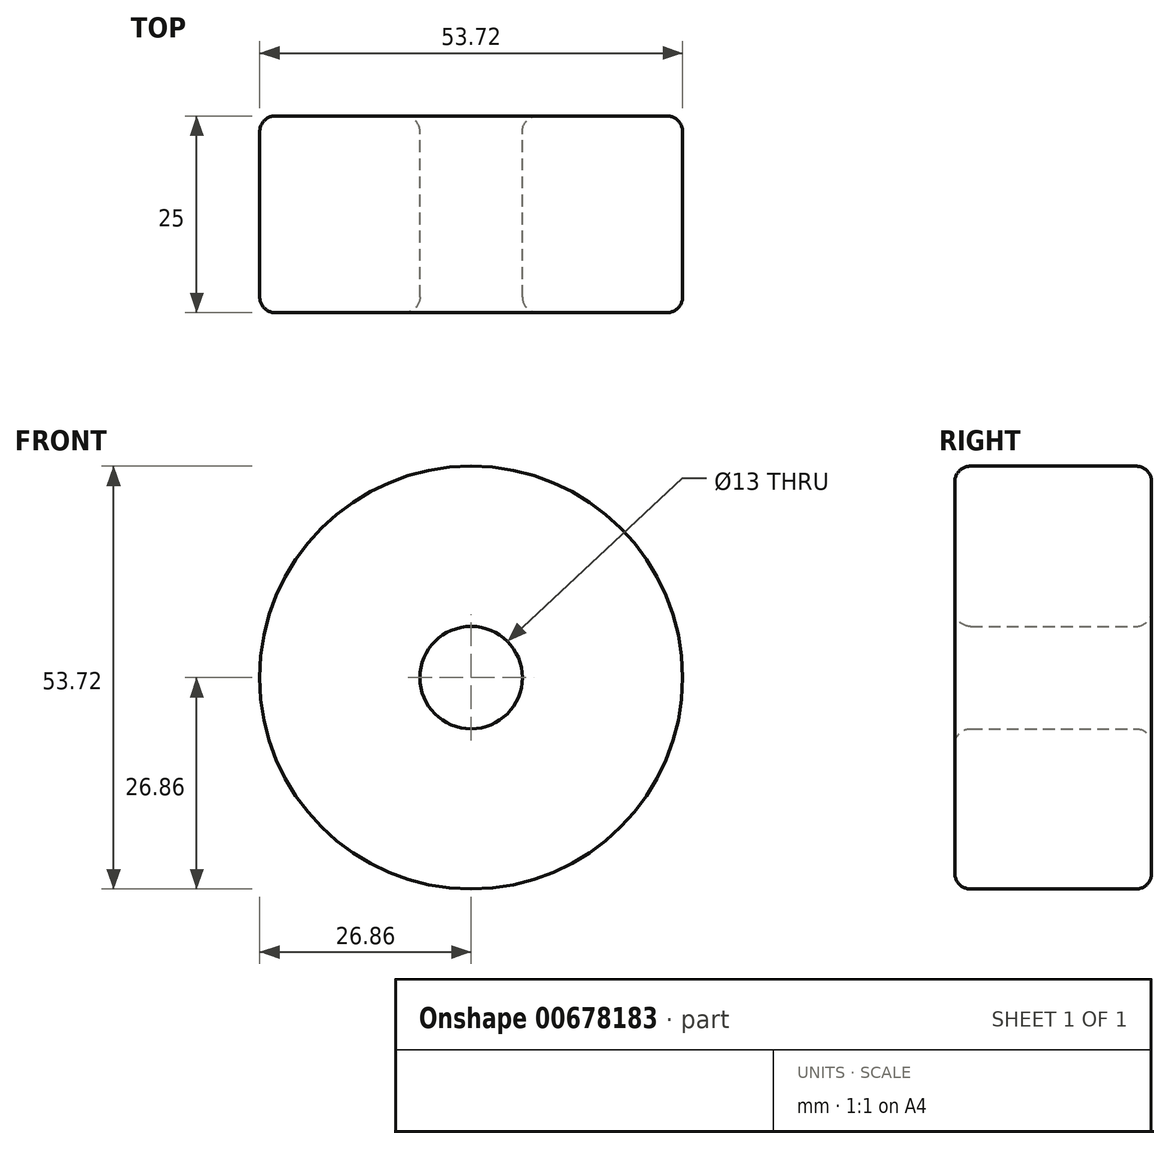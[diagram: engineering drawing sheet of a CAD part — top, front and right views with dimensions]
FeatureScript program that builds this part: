
annotation { "Feature Type Name" : "Feature", "Feature Type Description" : "" }
export const myFeature = defineFeature(function(context is Context, id is Id, definition is map)
    precondition{}
    {
        {
            var Q0;
            Q0=qCreatedBy(makeId("Front.planeOp"),FACE);
            var sketch = newSketch(context, id + "F0", { "sketchPlane" : qUnion([Q0])});
            skCircle(sketch, "E0", {"center": v(0, 0) * mm, "radius": 26.86 * mm});
            skCircle(sketch, "E1", {"center": v(0, 0) * mm, "radius": 29.34 * mm, "construction": true});
            skCircle(sketch, "E2", {"center": v(0, 0) * mm, "radius": 31.75 * mm, "construction": true});
            skLineSegment(sketch, "E3", {"start": v(0, 0) * mm, "end": v(0, 99.1) * mm, "construction": true});
            skLineSegment(sketch, "E4", {"start": v(0, 0) * mm, "end": v(-8, 122.09) * mm, "construction": true});
            skLineSegment(sketch, "E5", {"start": v(0, 29.34) * mm, "end": v(-120.67, 29.34) * mm, "construction": true});
            skLineSegment(sketch, "E6", {"start": v(0, 29.34) * mm, "end": v(-118.03, -13.62) * mm, "construction": true});
            skCircle(sketch, "E7", {"center": v(0, 0) * mm, "radius": 27.57 * mm, "construction": true});
            skCircle(sketch, "E8", {"center": v(0, 29.34) * mm, "radius": 14.6 * mm, "construction": true});
            skCircle(sketch, "E9", {"center": v(-13.72, 24.34) * mm, "radius": 14.6 * mm, "construction": true});
            skLineSegment(sketch, "E10", {"start": v(-4.16, 26.54) * mm, "end": v(-4.25, 26.52) * mm});
            skLineSegment(sketch, "E11", {"start": v(-4.25, 26.52) * mm, "end": v(-4.25, 26.52) * mm});
            skArc(sketch, "E12.MirrorCS", {"start": v(-4.25, 26.52) * mm, "mid": v(-4.23, 31.3) * mm, "end": v(-2.6, 35.79) * mm});
            skArc(sketch, "E13.MirrorCS", {"start": v(4.25, 26.52) * mm, "mid": v(4.23, 31.3) * mm, "end": v(2.6, 35.79) * mm});
            skLineSegment(sketch, "E14", {"start": v(-2.6, 35.79) * mm, "end": v(2.6, 35.79) * mm});
            skCircle(sketch, "E15", {"center": v(0, 0) * mm, "radius": 6.5 * mm});
            skSolve(sketch);
        }
        {
            var Q0;
            {var subQ1=sQuery(id+"F0.wireOp",EDGE,"NmizqAiV-zcEd-wW1i-qfzH-Hc12WR1YokAQ");Q0=makeQuery(id+"F0.imprint","IMPRINT",FACE,{"disambiguationData":[TD([[makeQuery(id+"F0.imprint","IMPRINT",EDGE,{"derivedFrom":subQ1}),1.0]])]});}
            var Q1;
            {var subQ0=sQuery(id+"F0.wireOp",EDGE,"E0");var subQ1=makeQuery(id+"F0.imprint","INTERSECT",VERTEX,{"derivedFrom":[subQ0,sQuery(id+"F0.wireOp",EDGE,"NmizqAiV-zcEd-wW1i-qfzH-Hc12WR1YokAQ")]});Q1=makeQuery(id+"F0.imprint","IMPRINT",FACE,{"disambiguationData":[TD([[makeQuery(id+"F0.imprint","IMPRINT",EDGE,{"disambiguationData":[TD([[subQ1,-1.0]])],"derivedFrom":subQ0}),1.0]])]});}
            var Q2;
            {var subQ1=sQuery(id+"F0.wireOp",EDGE,"E10");Q2=makeQuery(id+"F0.imprint","IMPRINT",FACE,{"disambiguationData":[TD([[makeQuery(id+"F0.imprint","IMPRINT",EDGE,{"derivedFrom":subQ1}),-1.0]])]});}
            extrude(context, id + "F1", {"entities" : qUnion([Q0, Q1, Q2]), "depth" : 25 * mm, "offsetDistance" : 25 * mm});
        }
        {
            var Q0;
            Q0=makeQuery(id+"F1.opExtrude","SWEPT_BODY",BODY,{"disambiguationData":[OSD([sQuery(id+"F0.wireOp",EDGE,"E0"),sQuery(id+"F0.wireOp",EDGE,"NmizqAiV-zcEd-wW1i-qfzH-Hc12WR1YokAQ"),sQuery(id+"F0.wireOp",EDGE,"fbdf0611-0ef5-4687-8596-0c79478fe7200.MirrorCS"),sQuery(id+"F0.wireOp",EDGE,"E10"),sQuery(id+"F0.wireOp",EDGE,"pZYjaMaG-vTmR-xlgZ-VFzj-i6ecItI8BHiG")])]});
            var Q1;
            Q1=makeQuery(id+"F1.opExtrude","SWEPT_FACE",FACE,{"disambiguationData":[OSD([sQuery(id+"F0.wireOp",EDGE,"E0")])]});
            circularPattern(context, id + "F2", {"operationType" : NewBodyOperationType.ADD, "entities" : qUnion([Q0]), "axis" : qUnion([Q1]), "angle" : 360 * degree, "instanceCount" : 12, "equalSpace" : true});
        }
        {
            var Q0;
            {var subQ0=makeQuery(id+"F1.opExtrude","CAP_FACE",FACE,{"disambiguationData":[OSD([sQuery(id+"F0.wireOp",EDGE,"E0"),sQuery(id+"F0.wireOp",EDGE,"E12.MirrorCS"),sQuery(id+"F0.wireOp",EDGE,"E13.MirrorCS"),sQuery(id+"F0.wireOp",EDGE,"E14")])],"isStart":false});Q0=makeQuery(id+"F2.boolean.opBoolean","MERGE",FACE,{"derivedFrom":[subQ0,makeQuery(id+"F2.opPattern","COPY",FACE,{"derivedFrom":subQ0,"instanceName":"1"}),makeQuery(id+"F2.opPattern","COPY",FACE,{"derivedFrom":subQ0,"instanceName":"2"}),makeQuery(id+"F2.opPattern","COPY",FACE,{"derivedFrom":subQ0,"instanceName":"3"}),makeQuery(id+"F2.opPattern","COPY",FACE,{"derivedFrom":subQ0,"instanceName":"4"}),makeQuery(id+"F2.opPattern","COPY",FACE,{"derivedFrom":subQ0,"instanceName":"5"}),makeQuery(id+"F2.opPattern","COPY",FACE,{"derivedFrom":subQ0,"instanceName":"6"}),makeQuery(id+"F2.opPattern","COPY",FACE,{"derivedFrom":subQ0,"instanceName":"7"}),makeQuery(id+"F2.opPattern","COPY",FACE,{"derivedFrom":subQ0,"instanceName":"8"}),makeQuery(id+"F2.opPattern","COPY",FACE,{"derivedFrom":subQ0,"instanceName":"9"}),makeQuery(id+"F2.opPattern","COPY",FACE,{"derivedFrom":subQ0,"instanceName":"10"}),makeQuery(id+"F2.opPattern","COPY",FACE,{"derivedFrom":subQ0,"instanceName":"11"})]});}
            var Q1;
            {var subQ0=makeQuery(id+"F1.opExtrude","CAP_FACE",FACE,{"disambiguationData":[OSD([sQuery(id+"F0.wireOp",EDGE,"E0"),sQuery(id+"F0.wireOp",EDGE,"E12.MirrorCS"),sQuery(id+"F0.wireOp",EDGE,"E13.MirrorCS"),sQuery(id+"F0.wireOp",EDGE,"E14")])],"isStart":true});Q1=makeQuery(id+"F2.boolean.opBoolean","MERGE",FACE,{"derivedFrom":[subQ0,makeQuery(id+"F2.opPattern","COPY",FACE,{"derivedFrom":subQ0,"instanceName":"1"}),makeQuery(id+"F2.opPattern","COPY",FACE,{"derivedFrom":subQ0,"instanceName":"2"}),makeQuery(id+"F2.opPattern","COPY",FACE,{"derivedFrom":subQ0,"instanceName":"3"}),makeQuery(id+"F2.opPattern","COPY",FACE,{"derivedFrom":subQ0,"instanceName":"4"}),makeQuery(id+"F2.opPattern","COPY",FACE,{"derivedFrom":subQ0,"instanceName":"5"}),makeQuery(id+"F2.opPattern","COPY",FACE,{"derivedFrom":subQ0,"instanceName":"6"}),makeQuery(id+"F2.opPattern","COPY",FACE,{"derivedFrom":subQ0,"instanceName":"7"}),makeQuery(id+"F2.opPattern","COPY",FACE,{"derivedFrom":subQ0,"instanceName":"8"}),makeQuery(id+"F2.opPattern","COPY",FACE,{"derivedFrom":subQ0,"instanceName":"9"}),makeQuery(id+"F2.opPattern","COPY",FACE,{"derivedFrom":subQ0,"instanceName":"10"}),makeQuery(id+"F2.opPattern","COPY",FACE,{"derivedFrom":subQ0,"instanceName":"11"})]});}
            fillet(context, id + "F3", {"entities" : qUnion([Q0, Q1]), "radius" : 2 * mm, "tangentPropagation" : true, "allowEdgeOverflow" : false});
        }
    });
